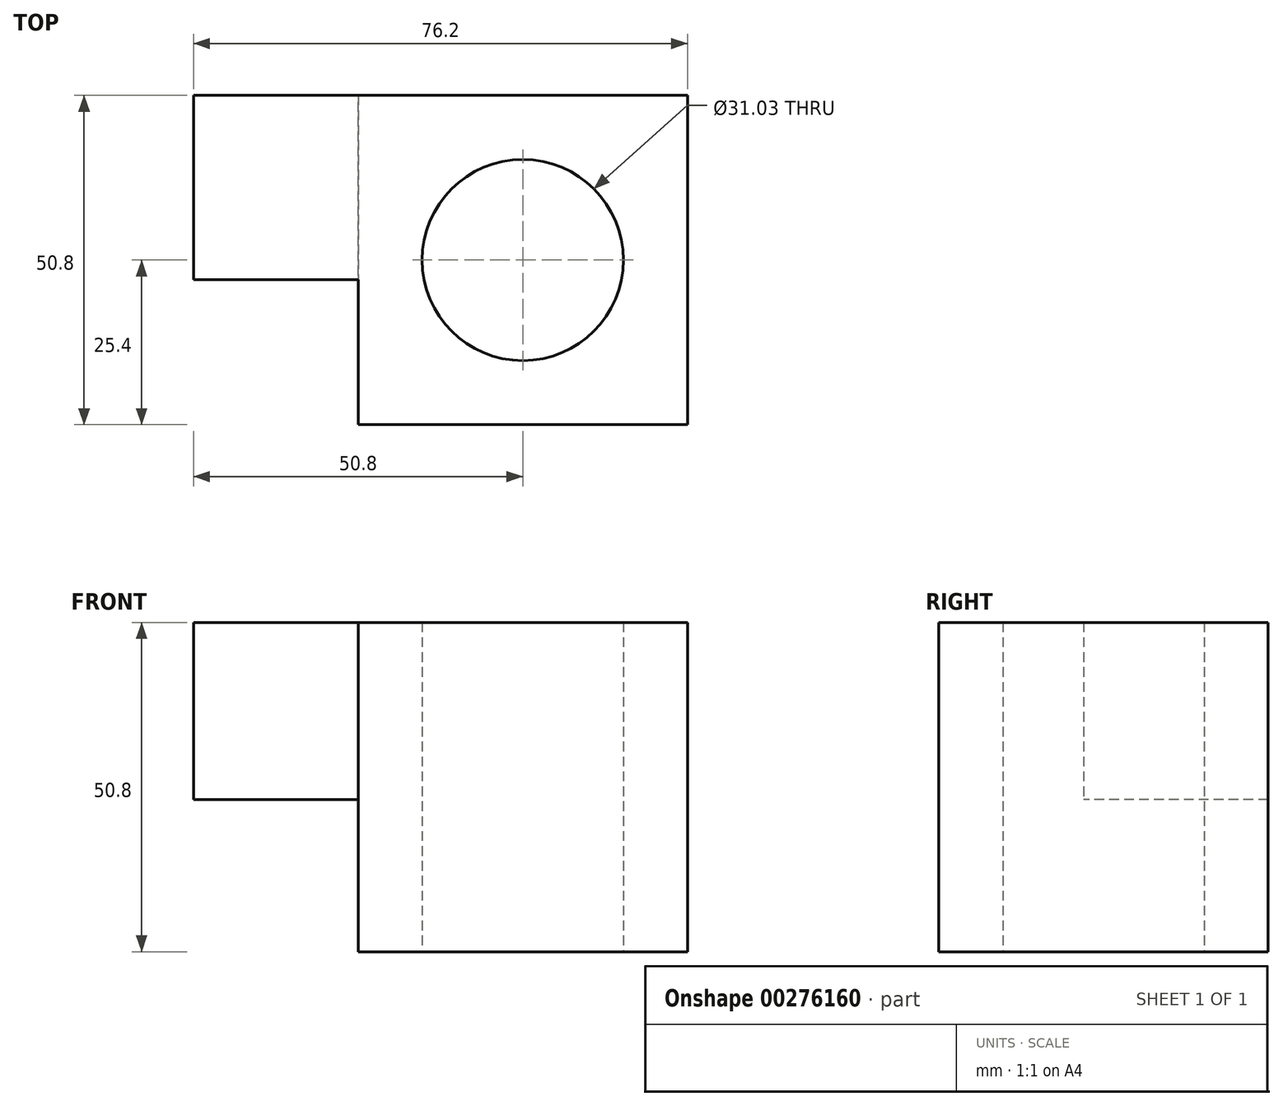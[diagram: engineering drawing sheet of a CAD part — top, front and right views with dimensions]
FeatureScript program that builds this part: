
annotation { "Feature Type Name" : "Feature", "Feature Type Description" : "" }
export const myFeature = defineFeature(function(context is Context, id is Id, definition is map)
    precondition{}
    {
        {
            var Q0;
            Q0=qCreatedBy(makeId("Front.planeOp"),FACE);
            var sketch = newSketch(context, id + "F0", { "sketchPlane" : qUnion([Q0])});
            skLineSegment(sketch, "E0.bottom", {"start": v(0, 0) * mm, "end": v(-50.8, 0) * mm});
            skLineSegment(sketch, "E0.top", {"start": v(0, 50.8) * mm, "end": v(-50.8, 50.8) * mm});
            skLineSegment(sketch, "E0.left", {"start": v(0, 0) * mm, "end": v(0, 50.8) * mm});
            skLineSegment(sketch, "E0.right", {"start": v(-50.8, 0) * mm, "end": v(-50.8, 50.8) * mm});
            skSolve(sketch);
        }
        {
            var Q0;
            Q0=makeQuery(id+"F0.imprint","IMPRINT",FACE,{"disambiguationData":[TD([[makeQuery(id+"F0.imprint","IMPRINT",EDGE,{"derivedFrom":sQuery(id+"F0.wireOp",EDGE,"E0.bottom")}),-1.0]])]});
            extrude(context, id + "F1", {"entities" : qUnion([Q0]), "depth" : 50.8 * mm});
        }
        {
            var Q0;
            Q0=makeQuery(id+"F1.opExtrude","SWEPT_FACE",FACE,{"disambiguationData":[OSD([sQuery(id+"F0.wireOp",EDGE,"E0.right")])]});
            var sketch = newSketch(context, id + "F2", { "sketchPlane" : qUnion([Q0])});
            skLineSegment(sketch, "E1.bottom", {"start": v(0, 50.8) * mm, "end": v(28.45, 50.8) * mm});
            skLineSegment(sketch, "E1.top", {"start": v(0, 23.5) * mm, "end": v(28.45, 23.5) * mm});
            skLineSegment(sketch, "E1.left", {"start": v(0, 50.8) * mm, "end": v(0, 23.5) * mm});
            skLineSegment(sketch, "E1.right", {"start": v(28.45, 50.8) * mm, "end": v(28.45, 23.5) * mm});
            skSolve(sketch);
        }
        {
            var Q0;
            Q0=makeQuery(id+"F2.imprint","IMPRINT",FACE,{"disambiguationData":[TD([[makeQuery(id+"F2.imprint","IMPRINT",EDGE,{"derivedFrom":sQuery(id+"F2.wireOp",EDGE,"E1.bottom")}),1.0]])]});
            extrude(context, id + "F3", {"entities" : qUnion([Q0]), "operationType" : NewBodyOperationType.ADD, "depth" : 25.4 * mm});
        }
        {
            var Q0;
            Q0=makeQuery(id+"F1.opExtrude","SWEPT_FACE",FACE,{"disambiguationData":[OSD([sQuery(id+"F0.wireOp",EDGE,"E0.bottom")])]});
            var sketch = newSketch(context, id + "F4", { "sketchPlane" : qUnion([Q0])});
            skCircle(sketch, "E2", {"center": v(-25.4, 25.4) * mm, "radius": 15.52 * mm});
            skSolve(sketch);
        }
        {
            var Q0;
            Q0 = qSketchRegion(id + "F4", true);
            extrude(context, id + "F5", {"entities" : qUnion([Q0]), "operationType" : NewBodyOperationType.REMOVE, "oppositeDirection" : true, "depth" : 50.8 * mm});
        }
    });
